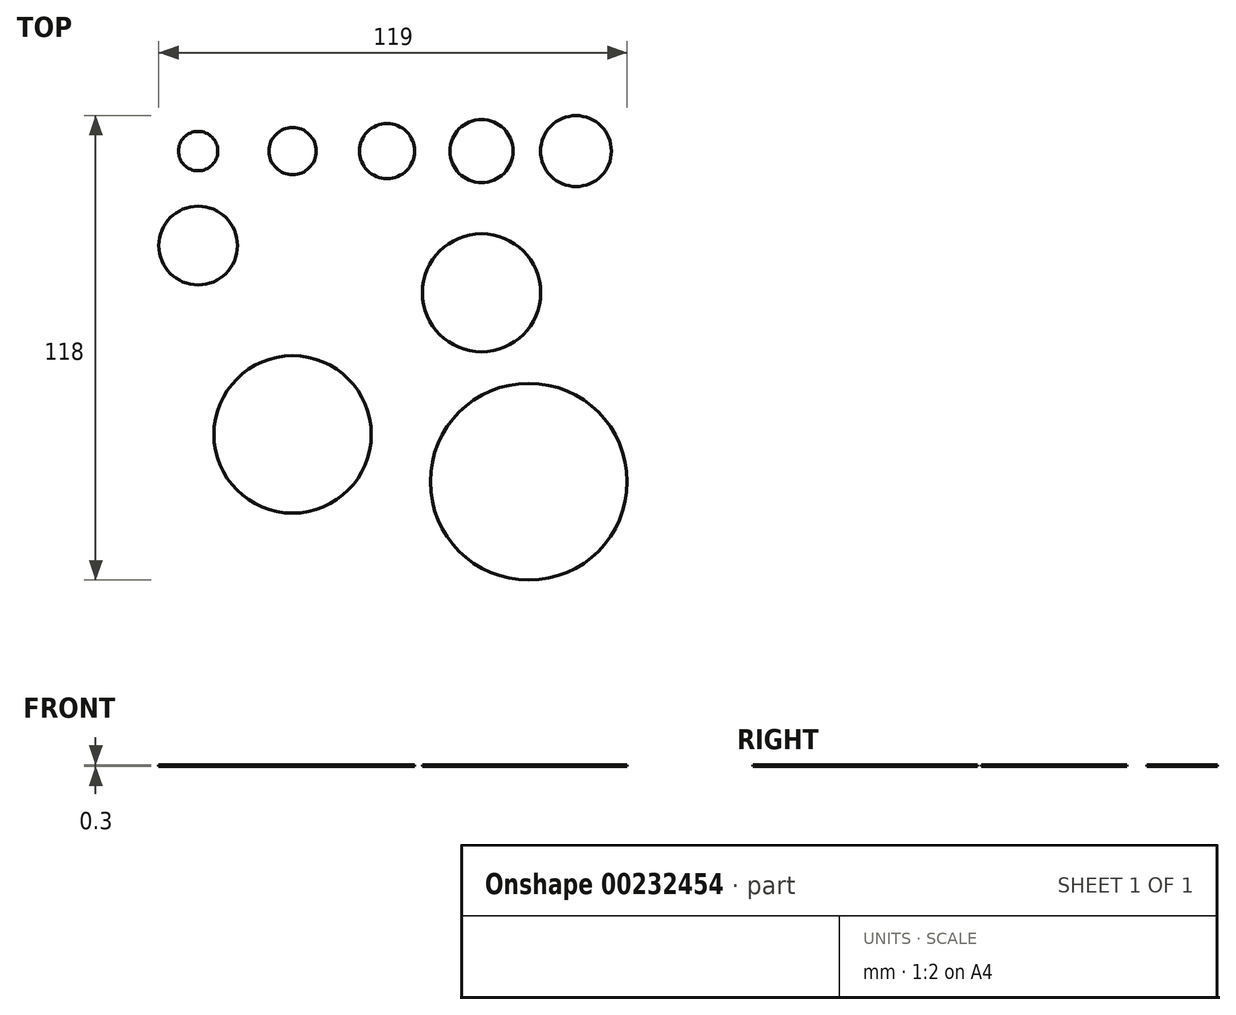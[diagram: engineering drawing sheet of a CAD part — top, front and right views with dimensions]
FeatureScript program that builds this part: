
annotation { "Feature Type Name" : "Feature", "Feature Type Description" : "" }
export const myFeature = defineFeature(function(context is Context, id is Id, definition is map)
    precondition{}
    {
        {
            var Q0;
            Q0=qCreatedBy(makeId("Top.planeOp"),FACE);
            var sketch = newSketch(context, id + "F0", { "sketchPlane" : qUnion([Q0])});
            skLineSegment(sketch, "E0.bottom", {"start": v(-60, 56.47) * mm, "end": v(60, 56.47) * mm, "construction": true});
            skLineSegment(sketch, "E0.top", {"start": v(-60, -63.53) * mm, "end": v(60, -63.53) * mm, "construction": true});
            skLineSegment(sketch, "E0.left", {"start": v(-60, 56.47) * mm, "end": v(-60, -63.53) * mm, "construction": true});
            skLineSegment(sketch, "E0.right", {"start": v(60, 56.47) * mm, "end": v(60, -63.53) * mm, "construction": true});
            skLineSegment(sketch, "E1", {"start": v(-48, 56.47) * mm, "end": v(-48, -63.53) * mm, "construction": true});
            skLineSegment(sketch, "E2", {"start": v(-36, 56.47) * mm, "end": v(-36, -63.53) * mm, "construction": true});
            skLineSegment(sketch, "E3", {"start": v(-24, 57.6) * mm, "end": v(-24, -63.53) * mm, "construction": true});
            skLineSegment(sketch, "E4", {"start": v(-12, 57.59) * mm, "end": v(-12, -63.53) * mm, "construction": true});
            skLineSegment(sketch, "E5", {"start": v(0, 57.6) * mm, "end": v(0, -62.25) * mm, "construction": true});
            skLineSegment(sketch, "E6", {"start": v(12, 57.68) * mm, "end": v(12, -62.15) * mm, "construction": true});
            skLineSegment(sketch, "E7", {"start": v(24, 57.64) * mm, "end": v(24, -62.15) * mm, "construction": true});
            skLineSegment(sketch, "E8", {"start": v(36, 57.6) * mm, "end": v(36, -62.54) * mm, "construction": true});
            skLineSegment(sketch, "E9", {"start": v(48, 57.64) * mm, "end": v(48, -63.53) * mm, "construction": true});
            skLineSegment(sketch, "E10", {"start": v(-60, 44.47) * mm, "end": v(60, 44.47) * mm, "construction": true});
            skLineSegment(sketch, "E11", {"start": v(-59.8, 32.47) * mm, "end": v(59.92, 32.47) * mm, "construction": true});
            skLineSegment(sketch, "E12", {"start": v(-59.83, 20.47) * mm, "end": v(60.03, 20.47) * mm, "construction": true});
            skLineSegment(sketch, "E13", {"start": v(-59.8, 8.47) * mm, "end": v(60.05, 8.47) * mm, "construction": true});
            skLineSegment(sketch, "E14", {"start": v(-59.83, -3.53) * mm, "end": v(60, -3.53) * mm, "construction": true});
            skLineSegment(sketch, "E15", {"start": v(-59.87, -15.53) * mm, "end": v(59.63, -15.53) * mm, "construction": true});
            skLineSegment(sketch, "E16", {"start": v(-59.82, -27.53) * mm, "end": v(60, -27.53) * mm, "construction": true});
            skLineSegment(sketch, "E17", {"start": v(-59.82, -39.53) * mm, "end": v(60, -39.53) * mm, "construction": true});
            skLineSegment(sketch, "E18", {"start": v(-59.8, -51.53) * mm, "end": v(60, -51.53) * mm, "construction": true});
            skCircle(sketch, "E19", {"center": v(-48, 44.47) * mm, "radius": 5 * mm});
            skCircle(sketch, "E20", {"center": v(-24, 44.47) * mm, "radius": 6 * mm});
            skCircle(sketch, "E21", {"center": v(0, 44.47) * mm, "radius": 7 * mm});
            skCircle(sketch, "E22", {"center": v(24, 44.47) * mm, "radius": 8 * mm});
            skCircle(sketch, "E23", {"center": v(48, 44.47) * mm, "radius": 9 * mm});
            skCircle(sketch, "E24", {"center": v(-48, 20.47) * mm, "radius": 10 * mm});
            skCircle(sketch, "E25", {"center": v(24, 8.47) * mm, "radius": 15 * mm});
            skCircle(sketch, "E26", {"center": v(-24, -27.53) * mm, "radius": 20 * mm});
            skCircle(sketch, "E27", {"center": v(36, -39.53) * mm, "radius": 25 * mm});
            skSolve(sketch);
        }
        {
            var Q0;
            Q0=makeQuery(id+"F0.imprint","IMPRINT",FACE,{"disambiguationData":[TD([[makeQuery(id+"F0.imprint","IMPRINT",EDGE,{"derivedFrom":sQuery(id+"F0.wireOp",EDGE,"E19")}),1.0]])]});
            var Q1;
            Q1=makeQuery(id+"F0.imprint","IMPRINT",FACE,{"disambiguationData":[TD([[makeQuery(id+"F0.imprint","IMPRINT",EDGE,{"derivedFrom":sQuery(id+"F0.wireOp",EDGE,"E24")}),1.0]])]});
            var Q2;
            Q2=makeQuery(id+"F0.imprint","IMPRINT",FACE,{"disambiguationData":[TD([[makeQuery(id+"F0.imprint","IMPRINT",EDGE,{"derivedFrom":sQuery(id+"F0.wireOp",EDGE,"E20")}),1.0]])]});
            var Q3;
            Q3=makeQuery(id+"F0.imprint","IMPRINT",FACE,{"disambiguationData":[TD([[makeQuery(id+"F0.imprint","IMPRINT",EDGE,{"derivedFrom":sQuery(id+"F0.wireOp",EDGE,"E21")}),1.0]])]});
            var Q4;
            Q4=makeQuery(id+"F0.imprint","IMPRINT",FACE,{"disambiguationData":[TD([[makeQuery(id+"F0.imprint","IMPRINT",EDGE,{"derivedFrom":sQuery(id+"F0.wireOp",EDGE,"E22")}),1.0]])]});
            var Q5;
            Q5=makeQuery(id+"F0.imprint","IMPRINT",FACE,{"disambiguationData":[TD([[makeQuery(id+"F0.imprint","IMPRINT",EDGE,{"derivedFrom":sQuery(id+"F0.wireOp",EDGE,"E23")}),1.0]])]});
            var Q6;
            Q6=makeQuery(id+"F0.imprint","IMPRINT",FACE,{"disambiguationData":[TD([[makeQuery(id+"F0.imprint","IMPRINT",EDGE,{"derivedFrom":sQuery(id+"F0.wireOp",EDGE,"E25")}),1.0]])]});
            var Q7;
            Q7=makeQuery(id+"F0.imprint","IMPRINT",FACE,{"disambiguationData":[TD([[makeQuery(id+"F0.imprint","IMPRINT",EDGE,{"derivedFrom":sQuery(id+"F0.wireOp",EDGE,"E26")}),1.0]])]});
            var Q8;
            Q8=makeQuery(id+"F0.imprint","IMPRINT",FACE,{"disambiguationData":[TD([[makeQuery(id+"F0.imprint","IMPRINT",EDGE,{"derivedFrom":sQuery(id+"F0.wireOp",EDGE,"E27")}),1.0]])]});
            extrude(context, id + "F1", {"entities" : qUnion([Q0, Q1, Q2, Q3, Q4, Q5, Q6, Q7, Q8]), "depth" : 0.3 * mm});
        }
    });
